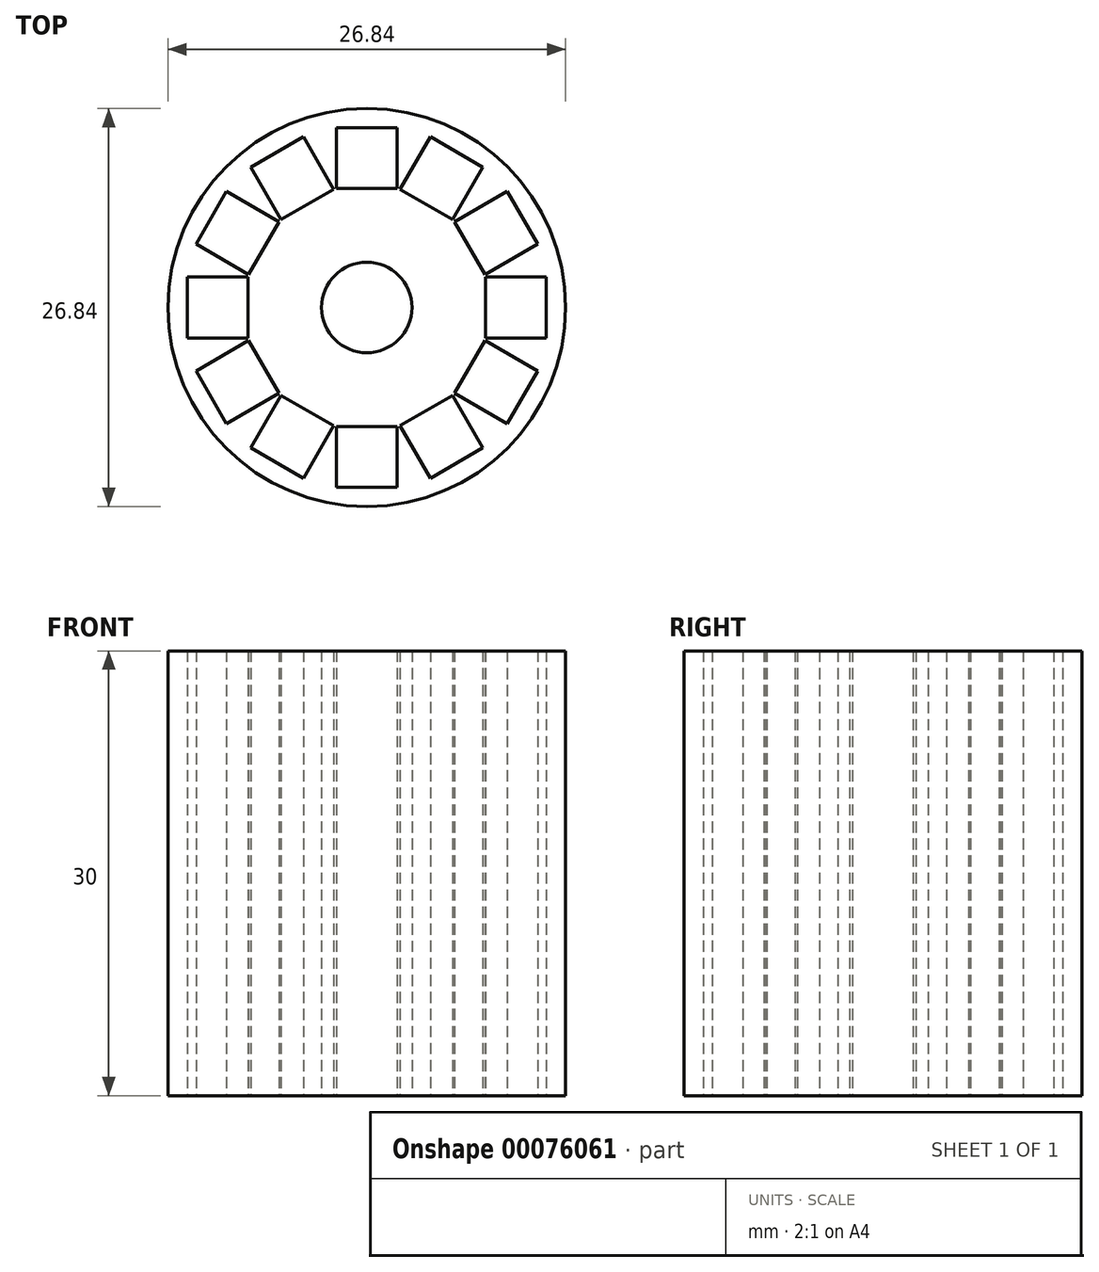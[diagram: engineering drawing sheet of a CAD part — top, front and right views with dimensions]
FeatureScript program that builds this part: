
annotation { "Feature Type Name" : "Feature", "Feature Type Description" : "" }
export const myFeature = defineFeature(function(context is Context, id is Id, definition is map)
    precondition{}
    {
        {
            var Q0;
            Q0=qCreatedBy(makeId("Top.planeOp"),FACE);
            var sketch = newSketch(context, id + "F0", { "sketchPlane" : qUnion([Q0])});
            skLineSegment(sketch, "E0", {"start": v(0, 0) * mm, "end": v(-4.9, 18.32) * mm});
            skLineSegment(sketch, "E1", {"start": v(-4.9, 18.32) * mm, "end": v(0, 0) * mm, "construction": true});
            skLineSegment(sketch, "E2", {"start": v(0, 0) * mm, "end": v(5.04, 18.8) * mm, "construction": true});
            skLineSegment(sketch, "E3", {"start": v(-2.15, 8.02) * mm, "end": v(2.15, 8.02) * mm});
            skLineSegment(sketch, "E4", {"start": v(0, 8.02) * mm, "end": v(0, 0) * mm});
            skLineSegment(sketch, "E5", {"start": v(-2.05, 8.02) * mm, "end": v(-2.05, 12.12) * mm});
            skLineSegment(sketch, "E6", {"start": v(-2.05, 12.12) * mm, "end": v(2.05, 12.12) * mm});
            skLineSegment(sketch, "E7", {"start": v(2.05, 12.12) * mm, "end": v(2.05, 8.02) * mm});
            skLineSegment(sketch, "E8.MirrorCS", {"start": v(5.87, 5.87) * mm, "end": v(2.15, 8.02) * mm});
            skLineSegment(sketch, "E9.MirrorCS", {"start": v(5.79, 5.92) * mm, "end": v(7.84, 9.47) * mm});
            skLineSegment(sketch, "E10.MirrorCS", {"start": v(7.84, 9.47) * mm, "end": v(4.29, 11.52) * mm});
            skLineSegment(sketch, "E11.MirrorCS", {"start": v(4.29, 11.52) * mm, "end": v(2.24, 7.97) * mm});
            skLineSegment(sketch, "E12.MirrorCS", {"start": v(13.41, 13.41) * mm, "end": v(0, 0) * mm, "construction": true});
            skLineSegment(sketch, "E13.MirrorCS", {"start": v(5.92, 5.79) * mm, "end": v(9.47, 7.84) * mm});
            skLineSegment(sketch, "E14.MirrorCS", {"start": v(9.47, 7.84) * mm, "end": v(11.52, 4.29) * mm});
            skLineSegment(sketch, "E15.MirrorCS", {"start": v(5.87, 5.87) * mm, "end": v(8.02, 2.15) * mm});
            skLineSegment(sketch, "E16.MirrorCS", {"start": v(11.52, 4.29) * mm, "end": v(7.97, 2.24) * mm});
            skLineSegment(sketch, "E17.MirrorCS", {"start": v(12.12, -2.05) * mm, "end": v(12.12, 2.05) * mm});
            skLineSegment(sketch, "E18.MirrorCS", {"start": v(12.12, 2.05) * mm, "end": v(8.02, 2.05) * mm});
            skLineSegment(sketch, "E19.MirrorCS", {"start": v(8.02, -2.15) * mm, "end": v(8.02, 2.15) * mm});
            skLineSegment(sketch, "E20.MirrorCS", {"start": v(8.02, -2.05) * mm, "end": v(12.12, -2.05) * mm});
            skLineSegment(sketch, "E21.MirrorCS", {"start": v(0, 0) * mm, "end": v(18.8, 5.04) * mm, "construction": true});
            skLineSegment(sketch, "E22.MirrorCS", {"start": v(18.32, -4.9) * mm, "end": v(0, 0) * mm, "construction": true});
            skLineSegment(sketch, "E23.MirrorCS", {"start": v(-12.12, -2.05) * mm, "end": v(-8.02, -2.05) * mm});
            skLineSegment(sketch, "E24.MirrorCS", {"start": v(-11.52, -4.29) * mm, "end": v(-7.97, -2.24) * mm});
            skLineSegment(sketch, "E25.MirrorCS", {"start": v(-5.92, -5.79) * mm, "end": v(-9.47, -7.84) * mm});
            skLineSegment(sketch, "E26.MirrorCS", {"start": v(-13.41, -13.41) * mm, "end": v(0, 0) * mm, "construction": true});
            skLineSegment(sketch, "E27.MirrorCS", {"start": v(-18.32, 4.9) * mm, "end": v(0, 0) * mm, "construction": true});
            skLineSegment(sketch, "E28.MirrorCS", {"start": v(-9.47, 7.84) * mm, "end": v(-5.92, 5.79) * mm});
            skLineSegment(sketch, "E29.MirrorCS", {"start": v(0, 0) * mm, "end": v(-18.8, -5.04) * mm, "construction": true});
            skLineSegment(sketch, "E30.MirrorCS", {"start": v(-4.29, 11.52) * mm, "end": v(-7.84, 9.47) * mm});
            skLineSegment(sketch, "E31.MirrorCS", {"start": v(-7.84, 9.47) * mm, "end": v(-5.79, 5.92) * mm});
            skLineSegment(sketch, "E32.MirrorCS", {"start": v(-2.24, 7.97) * mm, "end": v(-4.29, 11.52) * mm});
            skLineSegment(sketch, "E33.MirrorCS", {"start": v(-11.52, 4.29) * mm, "end": v(-9.47, 7.84) * mm});
            skLineSegment(sketch, "E34.MirrorCS", {"start": v(0, 0) * mm, "end": v(-13.77, 13.77) * mm, "construction": true});
            skLineSegment(sketch, "E35.MirrorCS", {"start": v(-7.97, 2.24) * mm, "end": v(-11.52, 4.29) * mm});
            skLineSegment(sketch, "E36.MirrorCS", {"start": v(-5.87, -5.87) * mm, "end": v(-8.02, -2.15) * mm});
            skLineSegment(sketch, "E37.MirrorCS", {"start": v(-4.01, 6.95) * mm, "end": v(0, 0) * mm});
            skLineSegment(sketch, "E38.MirrorCS", {"start": v(-8.02, 2.05) * mm, "end": v(-12.12, 2.05) * mm});
            skLineSegment(sketch, "E39.MirrorCS", {"start": v(-9.47, -7.84) * mm, "end": v(-11.52, -4.29) * mm});
            skLineSegment(sketch, "E40.MirrorCS", {"start": v(-2.15, 8.02) * mm, "end": v(-5.87, 5.87) * mm});
            skLineSegment(sketch, "E41.MirrorCS", {"start": v(-12.12, 2.05) * mm, "end": v(-12.12, -2.05) * mm});
            skLineSegment(sketch, "E42.MirrorCS", {"start": v(-8.02, 2.15) * mm, "end": v(-5.87, 5.87) * mm});
            skLineSegment(sketch, "E43.MirrorCS", {"start": v(-8.02, 2.15) * mm, "end": v(-8.02, -2.15) * mm});
            skLineSegment(sketch, "E44.MirrorCS", {"start": v(4.29, -11.52) * mm, "end": v(7.84, -9.47) * mm});
            skLineSegment(sketch, "E45.MirrorCS", {"start": v(11.52, -4.29) * mm, "end": v(9.47, -7.84) * mm});
            skLineSegment(sketch, "E46.MirrorCS", {"start": v(-4.29, -11.52) * mm, "end": v(-2.24, -7.97) * mm});
            skLineSegment(sketch, "E47.MirrorCS", {"start": v(-5.87, -5.87) * mm, "end": v(-2.15, -8.02) * mm});
            skLineSegment(sketch, "E48.MirrorCS", {"start": v(-2.05, -12.12) * mm, "end": v(-2.05, -8.02) * mm});
            skLineSegment(sketch, "E49.MirrorCS", {"start": v(-7.84, -9.47) * mm, "end": v(-4.29, -11.52) * mm});
            skLineSegment(sketch, "E50.MirrorCS", {"start": v(2.15, -8.02) * mm, "end": v(-2.15, -8.02) * mm});
            skLineSegment(sketch, "E51.MirrorCS", {"start": v(9.47, -7.84) * mm, "end": v(5.92, -5.79) * mm});
            skLineSegment(sketch, "E52.MirrorCS", {"start": v(2.24, -7.97) * mm, "end": v(4.29, -11.52) * mm});
            skLineSegment(sketch, "E53.MirrorCS", {"start": v(7.84, -9.47) * mm, "end": v(5.79, -5.92) * mm});
            skLineSegment(sketch, "E54.MirrorCS", {"start": v(2.05, -12.12) * mm, "end": v(-2.05, -12.12) * mm});
            skLineSegment(sketch, "E55.MirrorCS", {"start": v(2.05, -8.02) * mm, "end": v(2.05, -12.12) * mm});
            skLineSegment(sketch, "E56.MirrorCS", {"start": v(-5.79, -5.92) * mm, "end": v(-7.84, -9.47) * mm});
            skLineSegment(sketch, "E57.MirrorCS", {"start": v(2.15, -8.02) * mm, "end": v(5.87, -5.87) * mm});
            skLineSegment(sketch, "E58.MirrorCS", {"start": v(8.02, -2.15) * mm, "end": v(5.87, -5.87) * mm});
            skLineSegment(sketch, "E59.MirrorCS", {"start": v(7.97, -2.24) * mm, "end": v(11.52, -4.29) * mm});
            skCircle(sketch, "E60", {"center": v(0, 0) * mm, "radius": 13.42 * mm});
            skCircle(sketch, "E61", {"center": v(0, 0) * mm, "radius": 3.05 * mm});
            skSolve(sketch);
        }
        {
            var Q0;
            {var subQ0=sQuery(id+"F0.wireOp",EDGE,"E40.MirrorCS");var subQ2=sQuery(id+"F0.wireOp",EDGE,"E37.MirrorCS");var subQ3=makeQuery(id+"F0.imprint","INTERSECT",VERTEX,{"derivedFrom":[subQ2,subQ0]});Q0=makeQuery(id+"F0.imprint","IMPRINT",FACE,{"disambiguationData":[TD([[makeQuery(id+"F0.imprint","IMPRINT",EDGE,{"disambiguationData":[TD([[subQ3,-1.0]])],"derivedFrom":subQ2}),1.0]])]});}
            var Q1;
            {var subQ26=sQuery(id+"F0.wireOp",EDGE,"E4");var subQ27=sQuery(id+"F0.wireOp",EDGE,"E3");var subQ28=makeQuery(id+"F0.imprint","INTERSECT",VERTEX,{"derivedFrom":[subQ27,subQ26]});Q1=makeQuery(id+"F0.imprint","IMPRINT",FACE,{"disambiguationData":[TD([[makeQuery(id+"F0.imprint","IMPRINT",EDGE,{"disambiguationData":[TD([[subQ28,-1.0]])],"derivedFrom":subQ27}),-1.0]])]});}
            var Q2;
            {var subQ1=sQuery(id+"F0.wireOp",EDGE,"E3");var subQ5=sQuery(id+"F0.wireOp",EDGE,"E4");var subQ6=makeQuery(id+"F0.imprint","INTERSECT",VERTEX,{"derivedFrom":[subQ1,subQ5]});Q2=makeQuery(id+"F0.imprint","IMPRINT",FACE,{"disambiguationData":[TD([[makeQuery(id+"F0.imprint","IMPRINT",EDGE,{"disambiguationData":[TD([[subQ6,1.0]])],"derivedFrom":subQ1}),-1.0]])]});}
            var Q3;
            {var subQ30=sQuery(id+"F0.wireOp",EDGE,"E5");Q3=makeQuery(id+"F0.imprint","IMPRINT",FACE,{"disambiguationData":[TD([[makeQuery(id+"F0.imprint","IMPRINT",EDGE,{"derivedFrom":subQ30}),1.0]])]});}
            extrude(context, id + "F1", {"entities" : qUnion([Q0, Q1, Q2, Q3]), "depth" : 30 * mm});
        }
    });
